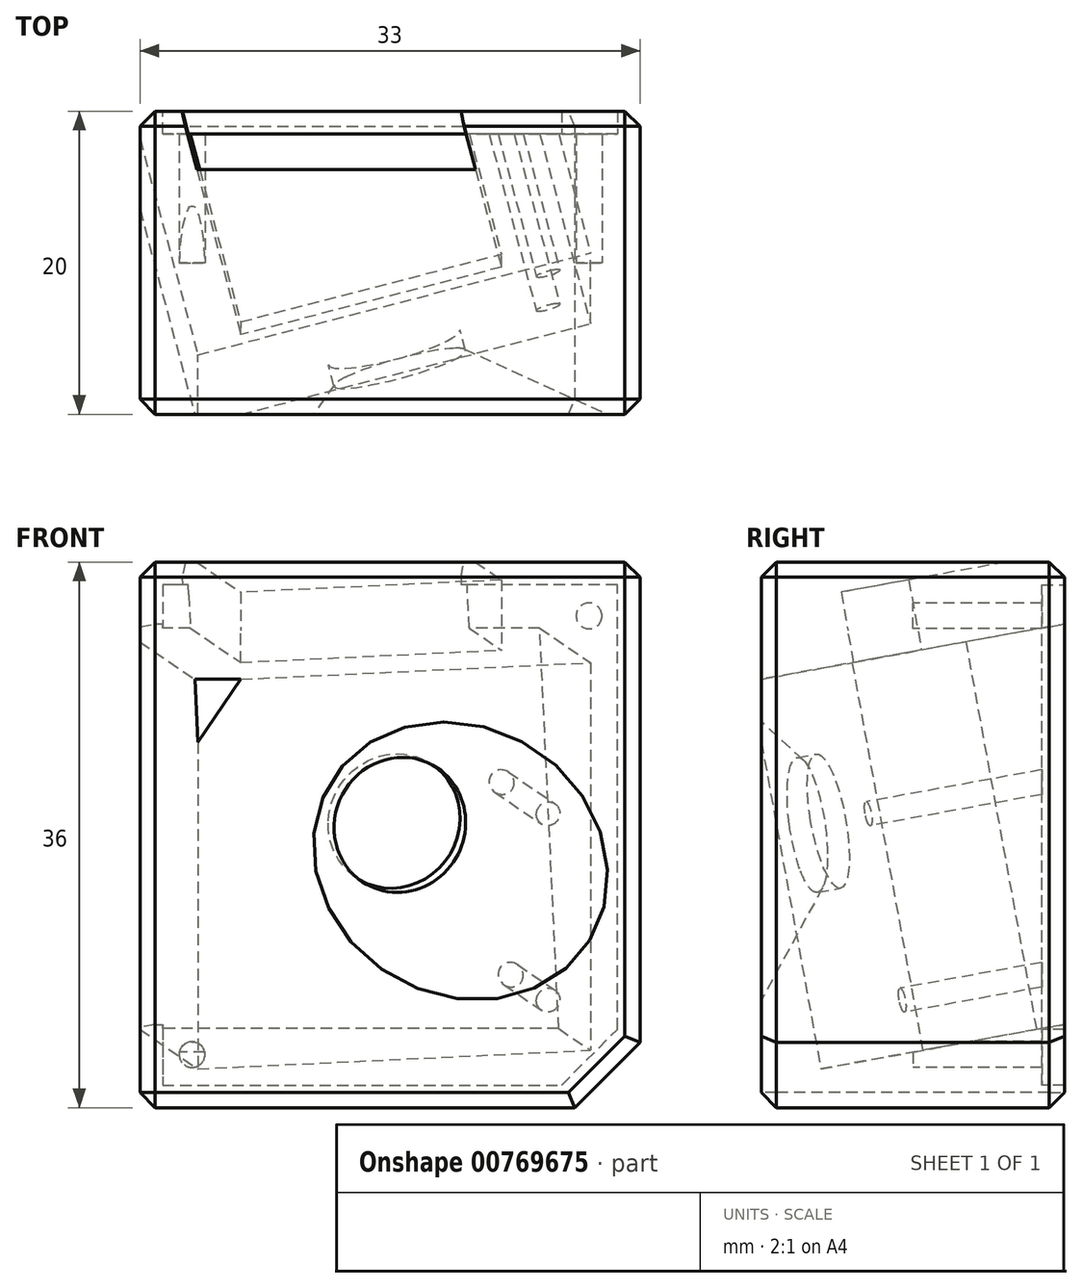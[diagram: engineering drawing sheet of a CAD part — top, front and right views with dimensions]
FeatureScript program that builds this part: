
annotation { "Feature Type Name" : "Feature", "Feature Type Description" : "" }
export const myFeature = defineFeature(function(context is Context, id is Id, definition is map)
    precondition{}
    {
        {
            var Q0;
            Q0=qCreatedBy(makeId("Top.planeOp"),FACE);
            var sketch = newSketch(context, id + "F0", { "sketchPlane" : qUnion([Q0])});
            skPoint(sketch, "E0.middle", {"position": v(0, 0) * mm});
            skLineSegment(sketch, "E1", {"start": v(-43.52, -6.53) * mm, "end": v(37.95, 15.3) * mm});
            skSolve(sketch);
        }
        {
            var Q0;
            Q0=qCreatedBy(makeId("Top.planeOp"),FACE);
            var Q1;
            Q1=sQuery(id+"F0.wireOp",EDGE,"E1");
            cPlane(context, id + "F1", {"entities" : qUnion([Q0, Q1]), "cplaneType" : CPlaneType.LINE_ANGLE, "offset" : 25 * mm, "angle" : 100 * degree, "width" : 150 * mm, "height" : 150 * mm});
        }
        {
            var Q0;
            Q0=qCreatedBy(id+"F1.planeOp",FACE);
            var sketch = newSketch(context, id + "F2", { "sketchPlane" : qUnion([Q0])});
            skLineSegment(sketch, "E2.bottom", {"start": v(13.4, 11.21) * mm, "end": v(-13.4, 11.21) * mm});
            skLineSegment(sketch, "E2.top", {"start": v(13.4, -14.79) * mm, "end": v(-13.4, -14.79) * mm});
            skLineSegment(sketch, "E2.left", {"start": v(13.4, 11.21) * mm, "end": v(13.4, -14.79) * mm});
            skLineSegment(sketch, "E2.right", {"start": v(-13.4, 11.21) * mm, "end": v(-13.4, -14.79) * mm});
            skLineSegment(sketch, "E3", {"start": v(0, 18.32) * mm, "end": v(0, -21.55) * mm, "construction": true});
            skPoint(sketch, "E3.startSnap0", {"position": v(0, 11.21) * mm});
            skCircle(sketch, "E4", {"center": v(0, 1.21) * mm, "radius": 4.5 * mm});
            skLineSegment(sketch, "E5", {"start": v(17.07, 1.21) * mm, "end": v(-22.2, 1.21) * mm, "construction": true});
            skCircle(sketch, "E6", {"center": v(10.5, 1.21) * mm, "radius": 0.8 * mm});
            skCircle(sketch, "E7", {"center": v(10.5, -11.29) * mm, "radius": 0.8 * mm});
            skLineSegment(sketch, "E8", {"start": v(7.51, 11.21) * mm, "end": v(7.51, -1.08) * mm});
            skLineSegment(sketch, "E9", {"start": v(7.51, -1.08) * mm, "end": v(10.43, -2.79) * mm});
            skLineSegment(sketch, "E10", {"start": v(10.43, -2.79) * mm, "end": v(10.43, -10.49) * mm});
            skLineSegment(sketch, "E11", {"start": v(10.5, -12.09) * mm, "end": v(0, -12.09) * mm});
            skLineSegment(sketch, "E12", {"start": v(8.9, 11.21) * mm, "end": v(8.9, 13.36) * mm});
            skLineSegment(sketch, "E13", {"start": v(8.9, 13.36) * mm, "end": v(-8.9, 13.36) * mm});
            skLineSegment(sketch, "E14", {"start": v(-8.9, 13.36) * mm, "end": v(-8.9, 11.21) * mm});
            skLineSegment(sketch, "E15.MirrorCS", {"start": v(-10.5, -12.09) * mm, "end": v(0, -12.09) * mm});
            skCircle(sketch, "E16.MirrorC", {"center": v(-10.5, -11.29) * mm, "radius": 0.8 * mm});
            skLineSegment(sketch, "E17.MirrorCS", {"start": v(-10.43, -2.79) * mm, "end": v(-10.43, -10.49) * mm});
            skLineSegment(sketch, "E18.MirrorCS", {"start": v(-7.51, 11.21) * mm, "end": v(-7.51, -1.08) * mm});
            skLineSegment(sketch, "E19.MirrorCS", {"start": v(-7.51, -1.08) * mm, "end": v(-10.43, -2.79) * mm});
            skCircle(sketch, "E20.MirrorC", {"center": v(-10.5, 1.21) * mm, "radius": 0.8 * mm});
            skLineSegment(sketch, "E21", {"start": v(-8.9, 13.36) * mm, "end": v(-8.9, 15.91) * mm});
            skLineSegment(sketch, "E22", {"start": v(-8.9, 15.91) * mm, "end": v(8.88, 15.91) * mm});
            skLineSegment(sketch, "E23", {"start": v(8.88, 15.91) * mm, "end": v(8.9, 13.36) * mm});
            skSolve(sketch);
        }
        {
            var Q0;
            Q0=qCreatedBy(makeId("Front.planeOp"),FACE);
            var sketch = newSketch(context, id + "F3", { "sketchPlane" : qUnion([Q0])});
            skLineSegment(sketch, "E24", {"start": v(14.98, 19.13) * mm, "end": v(14.98, -12.57) * mm});
            skLineSegment(sketch, "E25", {"start": v(-18.02, 19.13) * mm, "end": v(14.98, 19.13) * mm});
            skLineSegment(sketch, "E26", {"start": v(-18.02, 19.13) * mm, "end": v(-18.02, -16.87) * mm});
            skLineSegment(sketch, "E27", {"start": v(-18.02, -16.87) * mm, "end": v(10.68, -16.87) * mm});
            skLineSegment(sketch, "E28", {"start": v(10.68, -16.87) * mm, "end": v(14.98, -12.57) * mm});
            skLineSegment(sketch, "E29", {"start": v(13.48, 17.63) * mm, "end": v(-16.52, 17.63) * mm});
            skLineSegment(sketch, "E30", {"start": v(-16.52, 17.63) * mm, "end": v(-16.52, -15.37) * mm});
            skLineSegment(sketch, "E31", {"start": v(-16.52, -15.37) * mm, "end": v(9.8, -15.37) * mm});
            skLineSegment(sketch, "E32", {"start": v(9.8, -15.37) * mm, "end": v(13.48, -11.7) * mm});
            skLineSegment(sketch, "E33", {"start": v(13.48, -11.7) * mm, "end": v(13.48, 17.63) * mm});
            skCircle(sketch, "E34", {"center": v(11.62, 15.58) * mm, "radius": 0.85 * mm});
            skCircle(sketch, "E35", {"center": v(-14.58, -13.37) * mm, "radius": 0.85 * mm});
            skSolve(sketch);
        }
        {
            var Q0;
            Q0=makeQuery(id+"F3.imprint","IMPRINT",FACE,{"disambiguationData":[TD([[makeQuery(id+"F3.imprint","IMPRINT",EDGE,{"derivedFrom":sQuery(id+"F3.wireOp",EDGE,"E24")}),-1.0]])]});
            var Q1;
            Q1=makeQuery(id+"F3.imprint","IMPRINT",FACE,{"disambiguationData":[TD([[makeQuery(id+"F3.imprint","IMPRINT",EDGE,{"derivedFrom":sQuery(id+"F3.wireOp",EDGE,"E29")}),1.0]])]});
            var Q2;
            Q2=makeQuery(id+"F3.imprint","IMPRINT",FACE,{"disambiguationData":[TD([[makeQuery(id+"F3.imprint","IMPRINT",EDGE,{"derivedFrom":sQuery(id+"F3.wireOp",EDGE,"E34")}),1.0]])]});
            var Q3;
            Q3=makeQuery(id+"F3.imprint","IMPRINT",FACE,{"disambiguationData":[TD([[makeQuery(id+"F3.imprint","IMPRINT",EDGE,{"derivedFrom":sQuery(id+"F3.wireOp",EDGE,"E35")}),1.0]])]});
            extrude(context, id + "F4", {"entities" : qUnion([Q0, Q1, Q2, Q3]), "oppositeDirection" : true, "depth" : 20 * mm, "offsetDistance" : 25 * mm});
        }
        {
            var Q0;
            Q0=makeQuery(id+"F2.imprint","IMPRINT",FACE,{"disambiguationData":[TD([[makeQuery(id+"F2.imprint","IMPRINT",EDGE,{"derivedFrom":sQuery(id+"F2.wireOp",EDGE,"E4")}),1.0]])]});
            extrude(context, id + "F5", {"entities" : qUnion([Q0]), "operationType" : NewBodyOperationType.REMOVE, "oppositeDirection" : true, "depth" : 50 * mm, "offsetDistance" : 25 * mm});
        }
        {
            var Q0;
            Q0=makeQuery(id+"F2.imprint","IMPRINT",FACE,{"disambiguationData":[TD([[makeQuery(id+"F2.imprint","IMPRINT",EDGE,{"derivedFrom":sQuery(id+"F2.wireOp",EDGE,"E2.top")}),-1.0]])]});
            var Q1;
            Q1=makeQuery(id+"F2.imprint","IMPRINT",FACE,{"disambiguationData":[TD([[makeQuery(id+"F2.imprint","IMPRINT",EDGE,{"derivedFrom":sQuery(id+"F2.wireOp",EDGE,"E20.MirrorC")}),-1.0]])]});
            var Q2;
            Q2=makeQuery(id+"F2.imprint","IMPRINT",FACE,{"disambiguationData":[TD([[makeQuery(id+"F2.imprint","IMPRINT",EDGE,{"derivedFrom":sQuery(id+"F2.wireOp",EDGE,"E6")}),1.0]])]});
            var Q3;
            {var subQ0=sQuery(id+"F2.wireOp",EDGE,"E16.MirrorC");var subQ1=makeQuery(id+"F2.imprint","INTERSECT",VERTEX,{"derivedFrom":[sQuery(id+"F2.wireOp",EDGE,"E15.MirrorCS"),subQ0]});Q3=makeQuery(id+"F2.imprint","IMPRINT",FACE,{"disambiguationData":[TD([[makeQuery(id+"F2.imprint","IMPRINT",EDGE,{"disambiguationData":[TD([[subQ1,1.0]])],"derivedFrom":subQ0}),-1.0]])]});}
            var Q4;
            {var subQ0=sQuery(id+"F2.wireOp",EDGE,"E7");var subQ1=makeQuery(id+"F2.imprint","INTERSECT",VERTEX,{"derivedFrom":[subQ0,sQuery(id+"F2.wireOp",EDGE,"E10")]});Q4=makeQuery(id+"F2.imprint","IMPRINT",FACE,{"disambiguationData":[TD([[makeQuery(id+"F2.imprint","IMPRINT",EDGE,{"disambiguationData":[TD([[subQ1,-1.0]])],"derivedFrom":subQ0}),1.0]])]});}
            extrude(context, id + "F6", {"entities" : qUnion([Q0, Q1, Q2, Q3, Q4]), "operationType" : NewBodyOperationType.REMOVE, "depth" : 25 * mm, "offsetDistance" : 25 * mm, "hasSecondDirection" : true, "secondDirectionOppositeDirection" : false, "secondDirectionDepth" : 4 * mm});
        }
        {
            var Q0;
            Q0=makeQuery(id+"F2.imprint","IMPRINT",FACE,{"disambiguationData":[TD([[makeQuery(id+"F2.imprint","IMPRINT",EDGE,{"derivedFrom":sQuery(id+"F2.wireOp",EDGE,"E4")}),-1.0]])]});
            var Q1;
            Q1=makeQuery(id+"F2.imprint","IMPRINT",FACE,{"disambiguationData":[TD([[makeQuery(id+"F2.imprint","IMPRINT",EDGE,{"derivedFrom":sQuery(id+"F2.wireOp",EDGE,"E4")}),1.0]])]});
            var Q2;
            Q2=makeQuery(id+"F2.imprint","IMPRINT",FACE,{"disambiguationData":[TD([[makeQuery(id+"F2.imprint","IMPRINT",EDGE,{"derivedFrom":sQuery(id+"F2.wireOp",EDGE,"E6")}),1.0]])]});
            var Q3;
            Q3=makeQuery(id+"F2.imprint","IMPRINT",FACE,{"disambiguationData":[TD([[makeQuery(id+"F2.imprint","IMPRINT",EDGE,{"derivedFrom":sQuery(id+"F2.wireOp",EDGE,"E20.MirrorC")}),-1.0]])]});
            var Q4;
            {var subQ0=sQuery(id+"F2.wireOp",EDGE,"E16.MirrorC");var subQ1=makeQuery(id+"F2.imprint","INTERSECT",VERTEX,{"derivedFrom":[sQuery(id+"F2.wireOp",EDGE,"E15.MirrorCS"),subQ0]});Q4=makeQuery(id+"F2.imprint","IMPRINT",FACE,{"disambiguationData":[TD([[makeQuery(id+"F2.imprint","IMPRINT",EDGE,{"disambiguationData":[TD([[subQ1,1.0]])],"derivedFrom":subQ0}),-1.0]])]});}
            var Q5;
            {var subQ0=sQuery(id+"F2.wireOp",EDGE,"E7");var subQ1=makeQuery(id+"F2.imprint","INTERSECT",VERTEX,{"derivedFrom":[subQ0,sQuery(id+"F2.wireOp",EDGE,"E10")]});Q5=makeQuery(id+"F2.imprint","IMPRINT",FACE,{"disambiguationData":[TD([[makeQuery(id+"F2.imprint","IMPRINT",EDGE,{"disambiguationData":[TD([[subQ1,-1.0]])],"derivedFrom":subQ0}),1.0]])]});}
            extrude(context, id + "F7", {"entities" : qUnion([Q0, Q1, Q2, Q3, Q4, Q5]), "operationType" : NewBodyOperationType.REMOVE, "depth" : 25 * mm, "offsetDistance" : 25 * mm});
        }
        {
            var Q0;
            {var subQ4=sQuery(id+"F2.wireOp",EDGE,"E12");Q0=makeQuery(id+"F2.imprint","IMPRINT",FACE,{"disambiguationData":[TD([[makeQuery(id+"F2.imprint","IMPRINT",EDGE,{"derivedFrom":subQ4}),1.0]])]});}
            extrude(context, id + "F8", {"entities" : qUnion([Q0]), "operationType" : NewBodyOperationType.REMOVE, "depth" : 25 * mm, "offsetDistance" : 25 * mm, "hasSecondDirection" : true, "secondDirectionOppositeDirection" : false, "secondDirectionDepth" : 6 * mm});
        }
        {
            var Q0;
            Q0=makeQuery(id+"F2.imprint","IMPRINT",FACE,{"disambiguationData":[TD([[makeQuery(id+"F2.imprint","IMPRINT",EDGE,{"derivedFrom":sQuery(id+"F2.wireOp",EDGE,"E13")}),-1.0]])]});
            extrude(context, id + "F9", {"entities" : qUnion([Q0]), "operationType" : NewBodyOperationType.REMOVE, "depth" : 25 * mm, "offsetDistance" : 25 * mm, "hasSecondDirection" : true, "secondDirectionOppositeDirection" : false, "secondDirectionDepth" : 6 * mm});
        }
        {
            var Q0;
            Q0=sQuery(id+"F2.wireOp",EDGE,"E3");
            cPlane(context, id + "F10", {"entities" : qUnion([Q0]), "cplaneType" : CPlaneType.LINE_ANGLE, "offset" : 25 * mm, "angle" : 15 * degree, "oppositeDirection" : true, "width" : 150 * mm, "height" : 150 * mm});
        }
        {
            var Q0;
            Q0=qCreatedBy(id+"F10.planeOp",FACE);
            var sketch = newSketch(context, id + "F11", { "sketchPlane" : qUnion([Q0])});
            skLineSegment(sketch, "E36", {"start": v(-4.52, 2.17) * mm, "end": v(7.9, 0) * mm});
            skLineSegment(sketch, "E37", {"start": v(-4.44, -1.57) * mm, "end": v(2.98, -14.12) * mm});
            skLineSegment(sketch, "E38", {"start": v(2.98, -14.12) * mm, "end": v(5.94, 0.34) * mm});
            skLineSegment(sketch, "E39", {"start": v(-4.44, -1.57) * mm, "end": v(-3.81, 2.04) * mm});
            skSolve(sketch);
        }
        {
            var Q0;
            Q0=makeQuery(id+"F11.imprint","IMPRINT",FACE,{"disambiguationData":[TD([[makeQuery(id+"F11.imprint","IMPRINT",EDGE,{"derivedFrom":sQuery(id+"F11.wireOp",EDGE,"E37")}),1.0]])]});
            var Q1;
            Q1=sQuery(id+"F11.wireOp",EDGE,"E36");
            revolve(context, id + "F12", {"operationType" : NewBodyOperationType.REMOVE, "surfaceOperationType" : NewSurfaceOperationType.NEW, "entities" : qUnion([Q0]), "axis" : qUnion([Q1]), "revolveType" : RevolveType.FULL, "oppositeDirection" : true});
        }
        {
            var Q0;
            Q0=makeQuery(id+"F4.opExtrude","CAP_EDGE",EDGE,{"disambiguationData":[OSD([sQuery(id+"F3.wireOp",EDGE,"E27")])],"isStart":true});
            var Q1;
            Q1=makeQuery(id+"F4.opExtrude","CAP_EDGE",EDGE,{"disambiguationData":[OSD([sQuery(id+"F3.wireOp",EDGE,"E28")])],"isStart":true});
            var Q2;
            Q2=makeQuery(id+"F4.opExtrude","CAP_EDGE",EDGE,{"disambiguationData":[OSD([sQuery(id+"F3.wireOp",EDGE,"E24")])],"isStart":true});
            var Q3;
            Q3=makeQuery(id+"F4.opExtrude","CAP_EDGE",EDGE,{"disambiguationData":[OSD([sQuery(id+"F3.wireOp",EDGE,"E24")])],"isStart":false});
            var Q4;
            Q4=makeQuery(id+"F4.opExtrude","CAP_EDGE",EDGE,{"disambiguationData":[OSD([sQuery(id+"F3.wireOp",EDGE,"E28")])],"isStart":false});
            var Q5;
            Q5=makeQuery(id+"F4.opExtrude","CAP_EDGE",EDGE,{"disambiguationData":[OSD([sQuery(id+"F3.wireOp",EDGE,"E27")])],"isStart":false});
            var Q6;
            Q6=makeQuery(id+"F4.opExtrude","SWEPT_EDGE",EDGE,{"disambiguationData":[OSD([sQuery(id+"F3.wireOp",EDGE,"E25"),sQuery(id+"F3.wireOp",EDGE,"E26")])]});
            var Q7;
            Q7=makeQuery(id+"F4.opExtrude","SWEPT_EDGE",EDGE,{"disambiguationData":[OSD([sQuery(id+"F3.wireOp",EDGE,"E26"),sQuery(id+"F3.wireOp",EDGE,"E27")])]});
            var Q8;
            Q8=makeQuery(id+"F4.opExtrude","SWEPT_EDGE",EDGE,{"disambiguationData":[OSD([sQuery(id+"F3.wireOp",EDGE,"E24"),sQuery(id+"F3.wireOp",EDGE,"E25")])]});
            var Q9;
            Q9=makeQuery(id+"F4.opExtrude","CAP_EDGE",EDGE,{"disambiguationData":[OSD([sQuery(id+"F3.wireOp",EDGE,"E25")])],"isStart":true});
            var Q10;
            Q10=makeQuery(id+"F4.opExtrude","CAP_EDGE",EDGE,{"disambiguationData":[OSD([sQuery(id+"F3.wireOp",EDGE,"E26")])],"isStart":true});
            var Q11;
            {var subQ0=sQuery(id+"F3.wireOp",EDGE,"E25");var subQ1=sQuery(id+"F3.wireOp",EDGE,"E24");Q11=makeQuery(id+"F9.boolean.opBoolean","SPLIT",EDGE,{"disambiguationData":[TD([makeQuery(id+"F4.opExtrude","SWEPT_FACE",FACE,{"disambiguationData":[OSD([subQ1])]})])],"derivedFrom":makeQuery(id+"F4.opExtrude","CAP_EDGE",EDGE,{"disambiguationData":[OSD([subQ0])],"isStart":false})});}
            var Q12;
            {var subQ0=sQuery(id+"F3.wireOp",EDGE,"E26");var subQ1=sQuery(id+"F3.wireOp",EDGE,"E25");Q12=makeQuery(id+"F9.boolean.opBoolean","SPLIT",EDGE,{"disambiguationData":[TD([makeQuery(id+"F4.opExtrude","SWEPT_FACE",FACE,{"disambiguationData":[OSD([subQ0])]})])],"derivedFrom":makeQuery(id+"F4.opExtrude","CAP_EDGE",EDGE,{"disambiguationData":[OSD([subQ1])],"isStart":false})});}
            var Q13;
            {var subQ0=sQuery(id+"F3.wireOp",EDGE,"E27");var subQ1=sQuery(id+"F3.wireOp",EDGE,"E26");Q13=makeQuery(id+"F6.boolean.opBoolean","SPLIT",EDGE,{"disambiguationData":[TD([makeQuery(id+"F4.opExtrude","SWEPT_FACE",FACE,{"disambiguationData":[OSD([subQ0])]})])],"derivedFrom":makeQuery(id+"F4.opExtrude","CAP_EDGE",EDGE,{"disambiguationData":[OSD([subQ1])],"isStart":false})});}
            var Q14;
            {var subQ0=sQuery(id+"F3.wireOp",EDGE,"E26");var subQ1=sQuery(id+"F3.wireOp",EDGE,"E25");Q14=makeQuery(id+"F6.boolean.opBoolean","SPLIT",EDGE,{"disambiguationData":[TD([makeQuery(id+"F4.opExtrude","SWEPT_FACE",FACE,{"disambiguationData":[OSD([subQ1])]})])],"derivedFrom":makeQuery(id+"F4.opExtrude","CAP_EDGE",EDGE,{"disambiguationData":[OSD([subQ0])],"isStart":false})});}
            chamfer(context, id + "F13", {"entities" : qUnion([Q0, Q1, Q2, Q3, Q4, Q5, Q6, Q7, Q8, Q9, Q10, Q11, Q12, Q13, Q14]), "width" : 1 * mm, "tangentPropagation" : true});
        }
        {
            var Q0;
            Q0=makeQuery(id+"F3.imprint","IMPRINT",FACE,{"disambiguationData":[TD([[makeQuery(id+"F3.imprint","IMPRINT",EDGE,{"derivedFrom":sQuery(id+"F3.wireOp",EDGE,"E29")}),1.0]])]});
            extrude(context, id + "F14", {"entities" : qUnion([Q0]), "operationType" : NewBodyOperationType.REMOVE, "oppositeDirection" : true, "depth" : 25 * mm, "offsetDistance" : 25 * mm, "hasSecondDirection" : true, "secondDirectionOppositeDirection" : true, "secondDirectionDepth" : 18.5 * mm});
        }
        {
            var Q0;
            Q0=makeQuery(id+"F3.imprint","IMPRINT",FACE,{"disambiguationData":[TD([[makeQuery(id+"F3.imprint","IMPRINT",EDGE,{"derivedFrom":sQuery(id+"F3.wireOp",EDGE,"E34")}),1.0]])]});
            var Q1;
            Q1=makeQuery(id+"F3.imprint","IMPRINT",FACE,{"disambiguationData":[TD([[makeQuery(id+"F3.imprint","IMPRINT",EDGE,{"derivedFrom":sQuery(id+"F3.wireOp",EDGE,"E35")}),1.0]])]});
            extrude(context, id + "F15", {"entities" : qUnion([Q0, Q1]), "operationType" : NewBodyOperationType.REMOVE, "oppositeDirection" : true, "depth" : 25 * mm, "offsetDistance" : 25 * mm, "hasSecondDirection" : true, "secondDirectionOppositeDirection" : true, "secondDirectionDepth" : 10 * mm});
        }
    });
